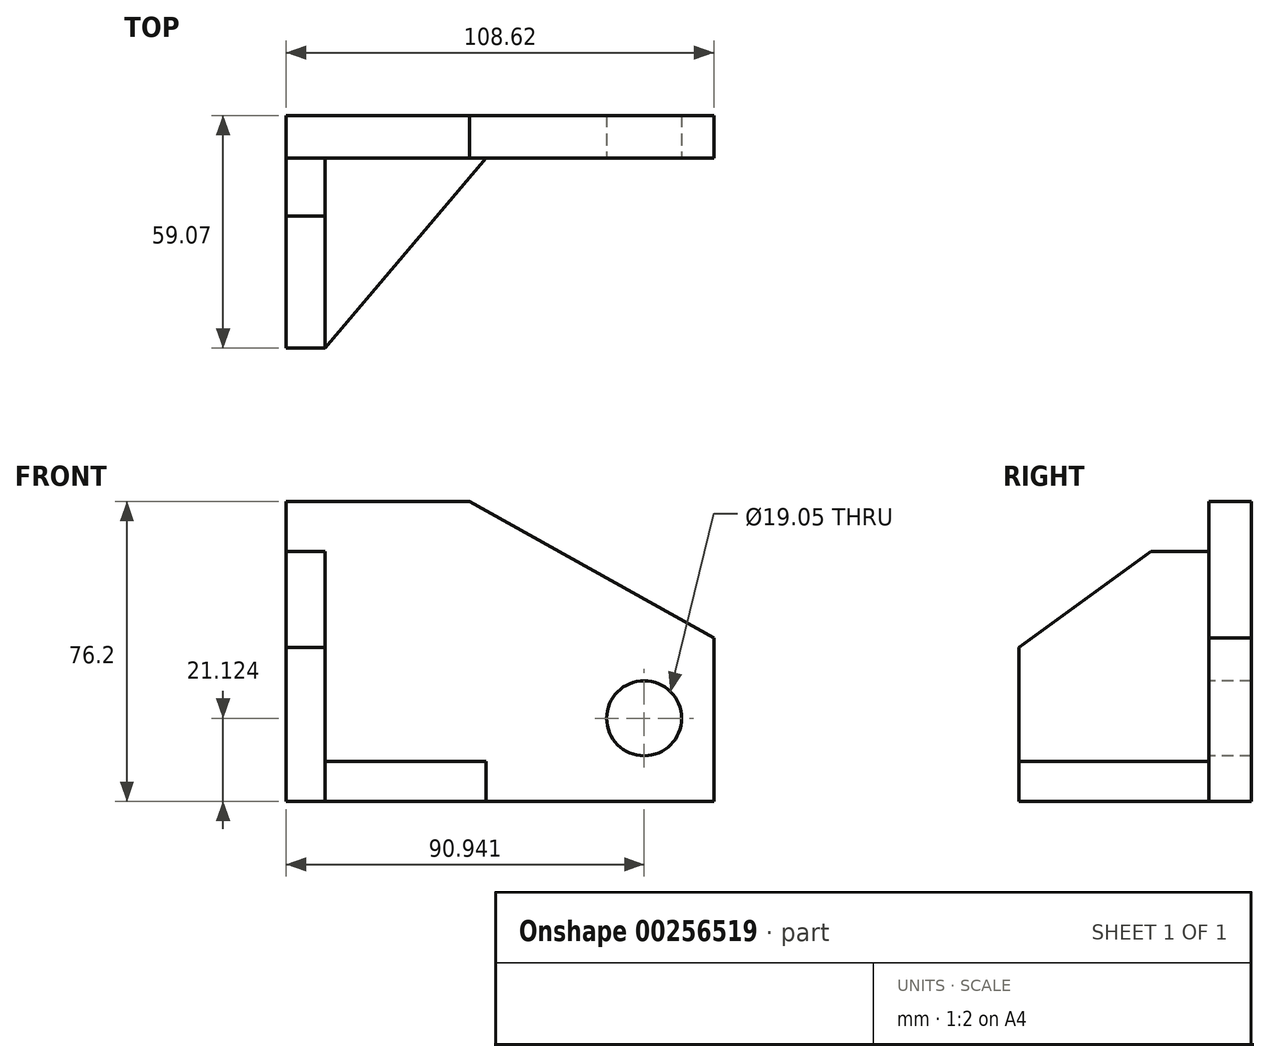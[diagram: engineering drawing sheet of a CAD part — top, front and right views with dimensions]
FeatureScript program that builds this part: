
annotation { "Feature Type Name" : "Feature", "Feature Type Description" : "" }
export const myFeature = defineFeature(function(context is Context, id is Id, definition is map)
    precondition{}
    {
        {
            var Q0;
            Q0=qCreatedBy(makeId("Top.planeOp"),FACE);
            var sketch = newSketch(context, id + "F0", { "sketchPlane" : qUnion([Q0])});
            skLineSegment(sketch, "E0.bottom", {"start": v(-50.82, 25.58) * mm, "end": v(57.8, 25.58) * mm});
            skLineSegment(sketch, "E0.top", {"start": v(-50.82, -33.5) * mm, "end": v(57.8, -33.5) * mm});
            skLineSegment(sketch, "E0.left", {"start": v(-50.82, 25.58) * mm, "end": v(-50.82, -33.5) * mm});
            skLineSegment(sketch, "E0.right", {"start": v(57.8, 25.58) * mm, "end": v(57.8, -33.5) * mm});
            skSolve(sketch);
        }
        {
            var Q0;
            Q0=makeQuery(id+"F0.imprint","IMPRINT",FACE,{"disambiguationData":[TD([[makeQuery(id+"F0.imprint","IMPRINT",EDGE,{"derivedFrom":sQuery(id+"F0.wireOp",EDGE,"E0.bottom")}),-1.0]])]});
            extrude(context, id + "F1", {"entities" : qUnion([Q0]), "depth" : 25.4 * mm});
        }
        {
            var Q0;
            Q0=makeQuery(id+"F1.opExtrude","CAP_FACE",FACE,{"disambiguationData":[OSD([sQuery(id+"F0.wireOp",EDGE,"E0.bottom"),sQuery(id+"F0.wireOp",EDGE,"E0.top"),sQuery(id+"F0.wireOp",EDGE,"E0.left"),sQuery(id+"F0.wireOp",EDGE,"E0.right")])],"isStart":false});
            var sketch = newSketch(context, id + "F2", { "sketchPlane" : qUnion([Q0])});
            skLineSegment(sketch, "E1.bottom", {"start": v(-50.82, 25.58) * mm, "end": v(57.8, 25.58) * mm});
            skLineSegment(sketch, "E1.top", {"start": v(-50.82, 14.73) * mm, "end": v(57.8, 14.73) * mm});
            skLineSegment(sketch, "E1.left", {"start": v(-50.82, 25.58) * mm, "end": v(-50.82, 14.73) * mm});
            skLineSegment(sketch, "E1.right", {"start": v(57.8, 25.58) * mm, "end": v(57.8, 14.73) * mm});
            skSolve(sketch);
        }
        {
            var Q0;
            Q0=makeQuery(id+"F2.imprint","IMPRINT",FACE,{"disambiguationData":[TD([[makeQuery(id+"F2.imprint","IMPRINT",EDGE,{"derivedFrom":sQuery(id+"F2.wireOp",EDGE,"E1.bottom")}),-1.0]])]});
            extrude(context, id + "F3", {"entities" : qUnion([Q0]), "operationType" : NewBodyOperationType.ADD, "depth" : 50.8 * mm});
        }
        {
            var Q0;
            Q0=makeQuery(id+"F1.opExtrude","CAP_FACE",FACE,{"disambiguationData":[OSD([sQuery(id+"F0.wireOp",EDGE,"E0.bottom"),sQuery(id+"F0.wireOp",EDGE,"E0.top"),sQuery(id+"F0.wireOp",EDGE,"E0.left"),sQuery(id+"F0.wireOp",EDGE,"E0.right")])],"isStart":false});
            var sketch = newSketch(context, id + "F4", { "sketchPlane" : qUnion([Q0])});
            skLineSegment(sketch, "E2.bottom", {"start": v(-50.82, 14.73) * mm, "end": v(-40.96, 14.73) * mm});
            skLineSegment(sketch, "E2.top", {"start": v(-50.82, -33.5) * mm, "end": v(-40.96, -33.5) * mm});
            skLineSegment(sketch, "E2.left", {"start": v(-50.82, 14.73) * mm, "end": v(-50.82, -33.5) * mm});
            skLineSegment(sketch, "E2.right", {"start": v(-40.96, 14.73) * mm, "end": v(-40.96, -33.5) * mm});
            skSolve(sketch);
        }
        {
            var Q0;
            Q0=makeQuery(id+"F4.imprint","IMPRINT",FACE,{"disambiguationData":[TD([[makeQuery(id+"F4.imprint","IMPRINT",EDGE,{"derivedFrom":sQuery(id+"F4.wireOp",EDGE,"E2.bottom")}),-1.0]])]});
            extrude(context, id + "F5", {"entities" : qUnion([Q0]), "operationType" : NewBodyOperationType.ADD, "depth" : 38.1 * mm});
        }
        {
            var Q0;
            Q0=makeQuery(id+"F5.opExtrude","SWEPT_FACE",FACE,{"disambiguationData":[OSD([sQuery(id+"F4.wireOp",EDGE,"E2.right")])]});
            var sketch = newSketch(context, id + "F6", { "sketchPlane" : qUnion([Q0])});
            skLineSegment(sketch, "E3", {"start": v(0, 63.5) * mm, "end": v(-33.5, 39.1) * mm});
            skSolve(sketch);
        }
        {
            var Q0;
            {var subQ0=sQuery(id+"F6.wireOp",EDGE,"E3");Q0=makeQuery(id+"F6.imprint","IMPRINT",FACE,{"disambiguationData":[TD([[makeQuery(id+"F6.imprint","IMPRINT",EDGE,{"derivedFrom":subQ0}),-1.0]])]});}
            extrude(context, id + "F7", {"entities" : qUnion([Q0]), "operationType" : NewBodyOperationType.REMOVE, "oppositeDirection" : true, "depth" : 25.4 * mm});
        }
        {
            var Q0;
            Q0=makeQuery(id+"F1.opExtrude","CAP_FACE",FACE,{"disambiguationData":[OSD([sQuery(id+"F0.wireOp",EDGE,"E0.bottom"),sQuery(id+"F0.wireOp",EDGE,"E0.top"),sQuery(id+"F0.wireOp",EDGE,"E0.left"),sQuery(id+"F0.wireOp",EDGE,"E0.right")])],"isStart":false});
            var sketch = newSketch(context, id + "F8", { "sketchPlane" : qUnion([Q0])});
            skLineSegment(sketch, "E4", {"start": v(0, 14.73) * mm, "end": v(-40.96, -33.5) * mm});
            skSolve(sketch);
        }
        {
            var Q0;
            {var subQ0=sQuery(id+"F8.wireOp",EDGE,"E4");Q0=makeQuery(id+"F8.imprint","IMPRINT",FACE,{"disambiguationData":[TD([[makeQuery(id+"F8.imprint","IMPRINT",EDGE,{"derivedFrom":subQ0}),1.0]])]});}
            extrude(context, id + "F9", {"entities" : qUnion([Q0]), "operationType" : NewBodyOperationType.REMOVE, "oppositeDirection" : true, "depth" : 25.4 * mm});
        }
        {
            var Q0;
            {var subQ0=sQuery(id+"F2.wireOp",EDGE,"E1.top");Q0=makeQuery(id+"F9.boolean.opBoolean","MERGE",FACE,{"derivedFrom":[makeQuery(id+"F3.opExtrude","SWEPT_FACE",FACE,{"disambiguationData":[OSD([subQ0])]}),makeQuery(id+"F9.opExtrude","SWEPT_FACE",FACE,{"disambiguationData":[OSD([subQ0])]})]});}
            var sketch = newSketch(context, id + "F10", { "sketchPlane" : qUnion([Q0])});
            skLineSegment(sketch, "E5", {"start": v(-4.3, 76.2) * mm, "end": v(57.8, 41.52) * mm});
            skSolve(sketch);
        }
        {
            var Q0;
            {var subQ0=sQuery(id+"F10.wireOp",EDGE,"E5");Q0=makeQuery(id+"F10.imprint","IMPRINT",FACE,{"disambiguationData":[TD([[makeQuery(id+"F10.imprint","IMPRINT",EDGE,{"derivedFrom":subQ0}),1.0]])]});}
            extrude(context, id + "F11", {"entities" : qUnion([Q0]), "operationType" : NewBodyOperationType.REMOVE, "oppositeDirection" : true, "depth" : 25.4 * mm});
        }
        {
            var Q0;
            {var subQ0=sQuery(id+"F2.wireOp",EDGE,"E1.top");Q0=makeQuery(id+"F9.boolean.opBoolean","MERGE",FACE,{"derivedFrom":[makeQuery(id+"F3.opExtrude","SWEPT_FACE",FACE,{"disambiguationData":[OSD([subQ0])]}),makeQuery(id+"F9.opExtrude","SWEPT_FACE",FACE,{"disambiguationData":[OSD([subQ0])]})]});}
            var sketch = newSketch(context, id + "F12", { "sketchPlane" : qUnion([Q0])});
            skCircle(sketch, "E6", {"center": v(40.12, 21.12) * mm, "radius": 10.12 * mm});
            skSolve(sketch);
        }
        {
            var Q0;
            Q0=sQuery(id+"F12.wireOp",VERTEX,"E6.center");
            var Q1;
            Q1=makeQuery(id+"F1.opExtrude","SWEPT_BODY",BODY,{"disambiguationData":[OSD([sQuery(id+"F0.wireOp",EDGE,"E0.bottom"),sQuery(id+"F0.wireOp",EDGE,"E0.top"),sQuery(id+"F0.wireOp",EDGE,"E0.left"),sQuery(id+"F0.wireOp",EDGE,"E0.right")])]});
            hole(context, id + "F13", {"style" : HoleStyle.SIMPLE, "endStyle" : HoleEndStyle.THROUGH, "holeDiameter" : 19.05 * mm, "tappedDepth" : 12.7 * mm, "tapClearance" : 3, "locations" : qUnion([Q0]), "scope" : qUnion([Q1])});
        }
        {
            var Q0;
            Q0=makeQuery(id+"F1.opExtrude","CAP_FACE",FACE,{"disambiguationData":[OSD([sQuery(id+"F0.wireOp",EDGE,"E0.bottom"),sQuery(id+"F0.wireOp",EDGE,"E0.top"),sQuery(id+"F0.wireOp",EDGE,"E0.left"),sQuery(id+"F0.wireOp",EDGE,"E0.right")])],"isStart":false});
            extrude(context, id + "F14", {"entities" : qUnion([Q0]), "operationType" : NewBodyOperationType.ADD, "oppositeDirection" : true, "depth" : 15.24 * mm});
        }
        {
            var Q0;
            Q0=makeQuery(id+"F1.opExtrude","CAP_FACE",FACE,{"disambiguationData":[OSD([sQuery(id+"F0.wireOp",EDGE,"E0.bottom"),sQuery(id+"F0.wireOp",EDGE,"E0.top"),sQuery(id+"F0.wireOp",EDGE,"E0.left"),sQuery(id+"F0.wireOp",EDGE,"E0.right")])],"isStart":false});
            var sketch = newSketch(context, id + "F15", { "sketchPlane" : qUnion([Q0])});
            skLineSegment(sketch, "E7", {"start": v(-40.96, 14.73) * mm, "end": v(-40.96, -33.5) * mm});
            skLineSegment(sketch, "E8", {"start": v(-40.96, -33.5) * mm, "end": v(0, 14.73) * mm});
            skLineSegment(sketch, "E9", {"start": v(0, 14.73) * mm, "end": v(-40.96, 14.73) * mm});
            skSolve(sketch);
        }
        {
            var Q0;
            Q0=makeQuery(id+"F15.imprint","IMPRINT",FACE,{"disambiguationData":[TD([[makeQuery(id+"F15.imprint","IMPRINT",EDGE,{"derivedFrom":sQuery(id+"F15.wireOp",EDGE,"E7")}),1.0]])]});
            extrude(context, id + "F16", {"entities" : qUnion([Q0]), "operationType" : NewBodyOperationType.REMOVE, "oppositeDirection" : true, "depth" : 15.24 * mm});
        }
    });
